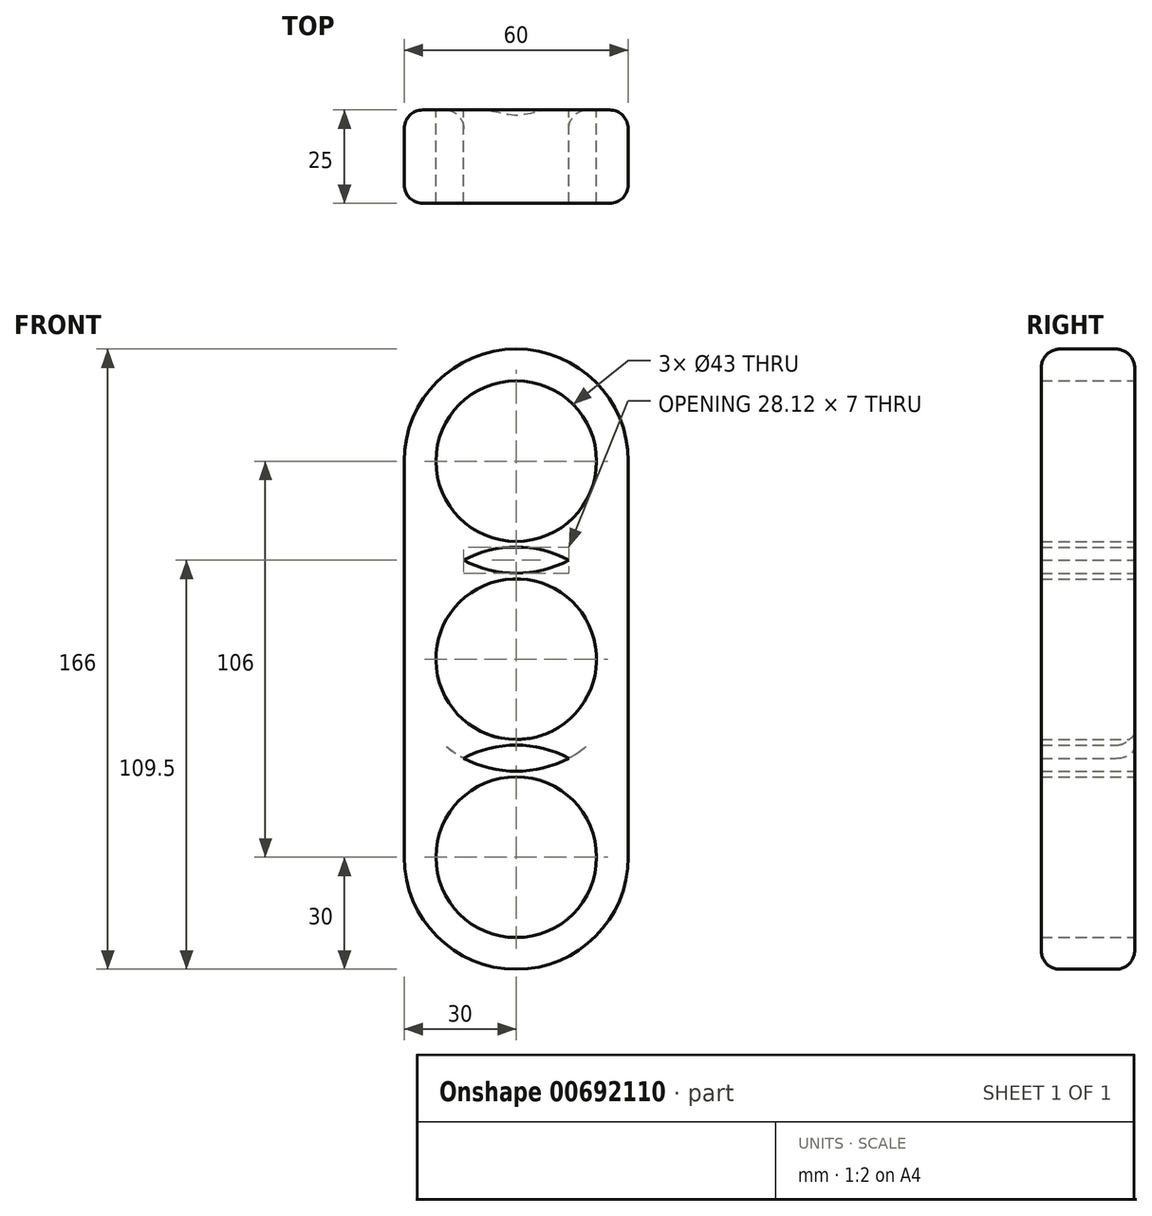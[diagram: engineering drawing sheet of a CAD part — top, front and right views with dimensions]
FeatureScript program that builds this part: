
annotation { "Feature Type Name" : "Feature", "Feature Type Description" : "" }
export const myFeature = defineFeature(function(context is Context, id is Id, definition is map)
    precondition{}
    {
        {
            var Q0;
            Q0=qCreatedBy(makeId("Front.planeOp"),FACE);
            var sketch = newSketch(context, id + "F0", { "sketchPlane" : qUnion([Q0])});
            skCircle(sketch, "E0", {"center": v(0, 0) * mm, "radius": 30 * mm});
            skCircle(sketch, "E1", {"center": v(0, 53) * mm, "radius": 30 * mm});
            skLineSegment(sketch, "E2", {"start": v(-30, 0) * mm, "end": v(-30, 53) * mm});
            skLineSegment(sketch, "E3", {"start": v(30, 0) * mm, "end": v(30, 53) * mm});
            skCircle(sketch, "E4.MirrorC", {"center": v(0, -53) * mm, "radius": 30 * mm});
            skLineSegment(sketch, "E5.MirrorCS", {"start": v(-30, 0) * mm, "end": v(-30, -53) * mm});
            skLineSegment(sketch, "E6.MirrorCS", {"start": v(30, 0) * mm, "end": v(30, -53) * mm});
            skCircle(sketch, "E7", {"center": v(0, 0) * mm, "radius": 21.5 * mm});
            skCircle(sketch, "E8", {"center": v(0, 53) * mm, "radius": 21.5 * mm});
            skCircle(sketch, "E9", {"center": v(0, -53) * mm, "radius": 21.5 * mm});
            skSolve(sketch);
        }
        {
            var Q0;
            Q0 = qSketchRegion(id + "F0", true);
            extrude(context, id + "F1", {"entities" : qUnion([Q0]), "depth" : 25 * mm, "offsetDistance" : 25 * mm});
        }
        {
            var Q0;
            Q0=makeQuery(id+"F1.opExtrude","CAP_EDGE",EDGE,{"disambiguationData":[OSD([sQuery(id+"F0.wireOp",EDGE,"E2"),sQuery(id+"F0.wireOp",EDGE,"E5.MirrorCS")])],"isStart":false});
            var Q1;
            Q1=makeQuery(id+"F1.opExtrude","CAP_EDGE",EDGE,{"disambiguationData":[OSD([sQuery(id+"F0.wireOp",EDGE,"E4.MirrorC")])],"isStart":true});
            fillet(context, id + "F2", {"entities" : qUnion([Q0, Q1]), "radius" : 5 * mm, "tangentPropagation" : true, "allowEdgeOverflow" : false});
        }
    });
